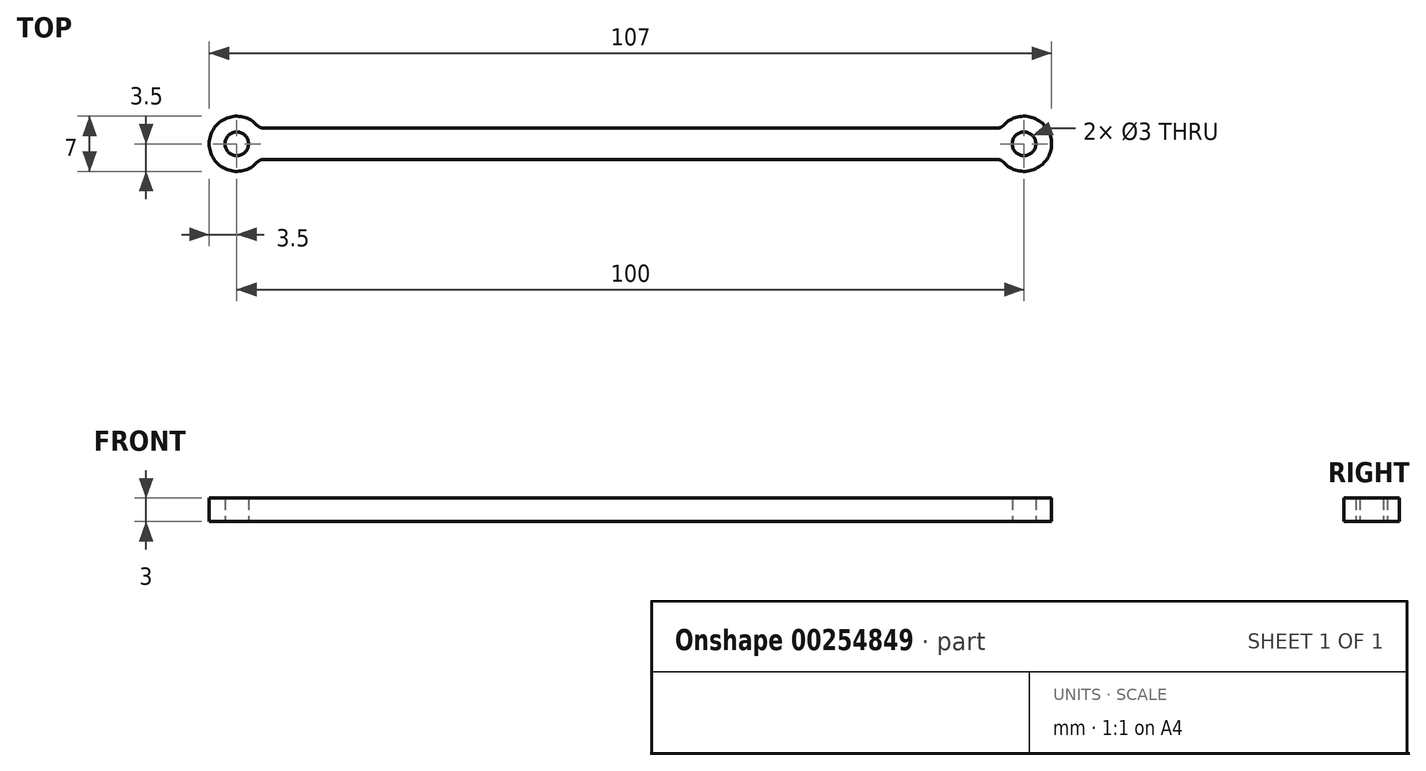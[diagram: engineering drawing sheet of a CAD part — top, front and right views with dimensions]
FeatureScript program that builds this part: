
annotation { "Feature Type Name" : "Feature", "Feature Type Description" : "" }
export const myFeature = defineFeature(function(context is Context, id is Id, definition is map)
    precondition{}
    {
        {
            var Q0;
            Q0=qCreatedBy(makeId("Top.planeOp"),FACE);
            var sketch = newSketch(context, id + "F0", { "sketchPlane" : qUnion([Q0])});
            skCircle(sketch, "E0", {"center": v(-50, 0) * mm, "radius": 1.5 * mm});
            skArc(sketch, "E1.0", {"start": v(-47.4, 2.33) * mm, "mid": v(-53.5, 0) * mm, "end": v(-47.4, -2.33) * mm});
            skLineSegment(sketch, "E2", {"start": v(-46.65, 2) * mm, "end": v(0, 2) * mm});
            skLineSegment(sketch, "E3", {"start": v(0, -2) * mm, "end": v(-46.65, -2) * mm});
            skPoint(sketch, "E4.visualSharp", {"position": v(-47.13, 2) * mm});
            skArc(sketch, "E4.filletArc", {"start": v(-47.4, 2.33) * mm, "mid": v(-47.05, 2.09) * mm, "end": v(-46.65, 2) * mm});
            skPoint(sketch, "E5.visualSharp", {"position": v(-47.13, -2) * mm});
            skArc(sketch, "E5.filletArc", {"start": v(-46.65, -2) * mm, "mid": v(-47.05, -2.09) * mm, "end": v(-47.4, -2.33) * mm});
            skLineSegment(sketch, "E6.MirrorCS", {"start": v(46.65, 2) * mm, "end": v(0, 2) * mm});
            skLineSegment(sketch, "E7.MirrorCS", {"start": v(0, -2) * mm, "end": v(46.65, -2) * mm});
            skArc(sketch, "E8.MirrorCS", {"start": v(46.65, -2) * mm, "mid": v(47.05, -2.09) * mm, "end": v(47.4, -2.33) * mm});
            skCircle(sketch, "E9.MirrorC", {"center": v(50, 0) * mm, "radius": 1.5 * mm});
            skArc(sketch, "E10.MirrorCS", {"start": v(47.4, 2.33) * mm, "mid": v(53.5, 0) * mm, "end": v(47.4, -2.33) * mm});
            skArc(sketch, "E11.MirrorCS", {"start": v(47.4, 2.33) * mm, "mid": v(47.05, 2.09) * mm, "end": v(46.65, 2) * mm});
            skSolve(sketch);
        }
        {
            var Q0;
            Q0 = qSketchRegion(id + "F0", true);
            extrude(context, id + "F1", {"entities" : qUnion([Q0]), "depth" : 3 * mm, "symmetric" : true});
        }
    });
